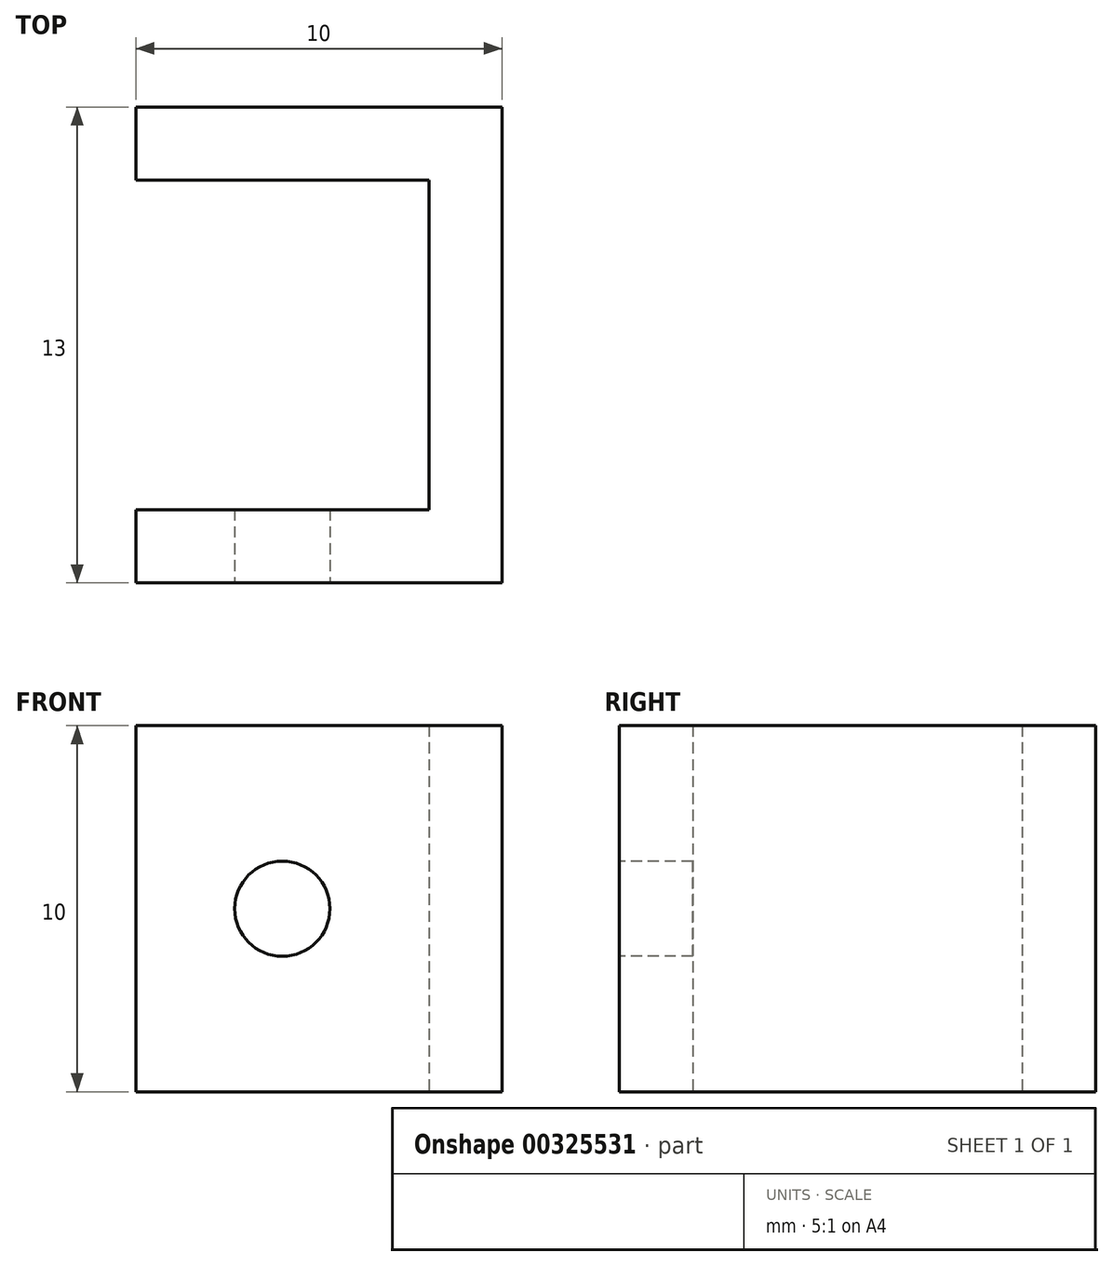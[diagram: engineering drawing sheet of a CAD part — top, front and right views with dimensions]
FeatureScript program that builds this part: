
annotation { "Feature Type Name" : "Feature", "Feature Type Description" : "" }
export const myFeature = defineFeature(function(context is Context, id is Id, definition is map)
    precondition{}
    {
        {
            var Q0;
            Q0=qCreatedBy(makeId("Top.planeOp"),FACE);
            var sketch = newSketch(context, id + "F0", { "sketchPlane" : qUnion([Q0])});
            skLineSegment(sketch, "E0.bottom", {"start": v(5, -6.5) * mm, "end": v(-5, -6.5) * mm});
            skLineSegment(sketch, "E0.top", {"start": v(5, 6.5) * mm, "end": v(-5, 6.5) * mm});
            skLineSegment(sketch, "E0.left", {"start": v(5, -6.5) * mm, "end": v(5, 6.5) * mm});
            skLineSegment(sketch, "E0.right", {"start": v(-5, -6.5) * mm, "end": v(-5, 6.5) * mm});
            skPoint(sketch, "E0.middle", {"position": v(0, 0) * mm});
            skLineSegment(sketch, "E1.bottom", {"start": v(3, -4.5) * mm, "end": v(-3, -4.5) * mm});
            skLineSegment(sketch, "E1.top", {"start": v(3, 4.5) * mm, "end": v(-3, 4.5) * mm});
            skLineSegment(sketch, "E1.left", {"start": v(3, -4.5) * mm, "end": v(3, 4.5) * mm});
            skLineSegment(sketch, "E1.right", {"start": v(-3, -4.5) * mm, "end": v(-3, 4.5) * mm});
            skLineSegment(sketch, "E2", {"start": v(-3, 4.5) * mm, "end": v(-5, 4.5) * mm});
            skLineSegment(sketch, "E3", {"start": v(-3, -4.5) * mm, "end": v(-5, -4.5) * mm});
            skSolve(sketch);
        }
        {
            var Q0;
            {var subQ1=sQuery(id+"F0.wireOp",EDGE,"E0.bottom");Q0=makeQuery(id+"F0.imprint","IMPRINT",FACE,{"disambiguationData":[TD([[makeQuery(id+"F0.imprint","IMPRINT",EDGE,{"derivedFrom":subQ1}),-1.0]])]});}
            extrude(context, id + "F1", {"entities" : qUnion([Q0]), "depth" : 10 * mm});
        }
        {
            var Q0;
            Q0=makeQuery(id+"F1.opExtrude","SWEPT_FACE",FACE,{"disambiguationData":[OSD([sQuery(id+"F0.wireOp",EDGE,"E0.bottom")])]});
            var sketch = newSketch(context, id + "F2", { "sketchPlane" : qUnion([Q0])});
            skLineSegment(sketch, "E4.0.0", {"start": v(-5, 0) * mm, "end": v(5, 0) * mm});
            skLineSegment(sketch, "E4.0.1", {"start": v(5, 0) * mm, "end": v(5, 10) * mm});
            skLineSegment(sketch, "E4.0.2", {"start": v(5, 10) * mm, "end": v(-5, 10) * mm});
            skLineSegment(sketch, "E4.0.3", {"start": v(-5, 10) * mm, "end": v(-5, 0) * mm});
            skCircle(sketch, "E5", {"center": v(-1, 5) * mm, "radius": 1.3 * mm});
            skSolve(sketch);
        }
        {
            var Q0;
            Q0=makeQuery(id+"F2.imprint","IMPRINT",FACE,{"disambiguationData":[TD([[makeQuery(id+"F2.imprint","IMPRINT",EDGE,{"derivedFrom":sQuery(id+"F2.wireOp",EDGE,"NgOUmwW7-8U8m-MLwP-BjeM-vhEjkkgO5p01")}),1.0]])]});
            var Q1;
            Q1=makeQuery(id+"F2.imprint","IMPRINT",FACE,{"disambiguationData":[TD([[makeQuery(id+"F2.imprint","IMPRINT",EDGE,{"derivedFrom":sQuery(id+"F2.wireOp",EDGE,"E5")}),1.0]])]});
            extrude(context, id + "F3", {"entities" : qUnion([Q0, Q1]), "operationType" : NewBodyOperationType.REMOVE, "endBound" : BoundingType.UP_TO_NEXT, "oppositeDirection" : true, "depth" : 25 * mm});
        }
    });
